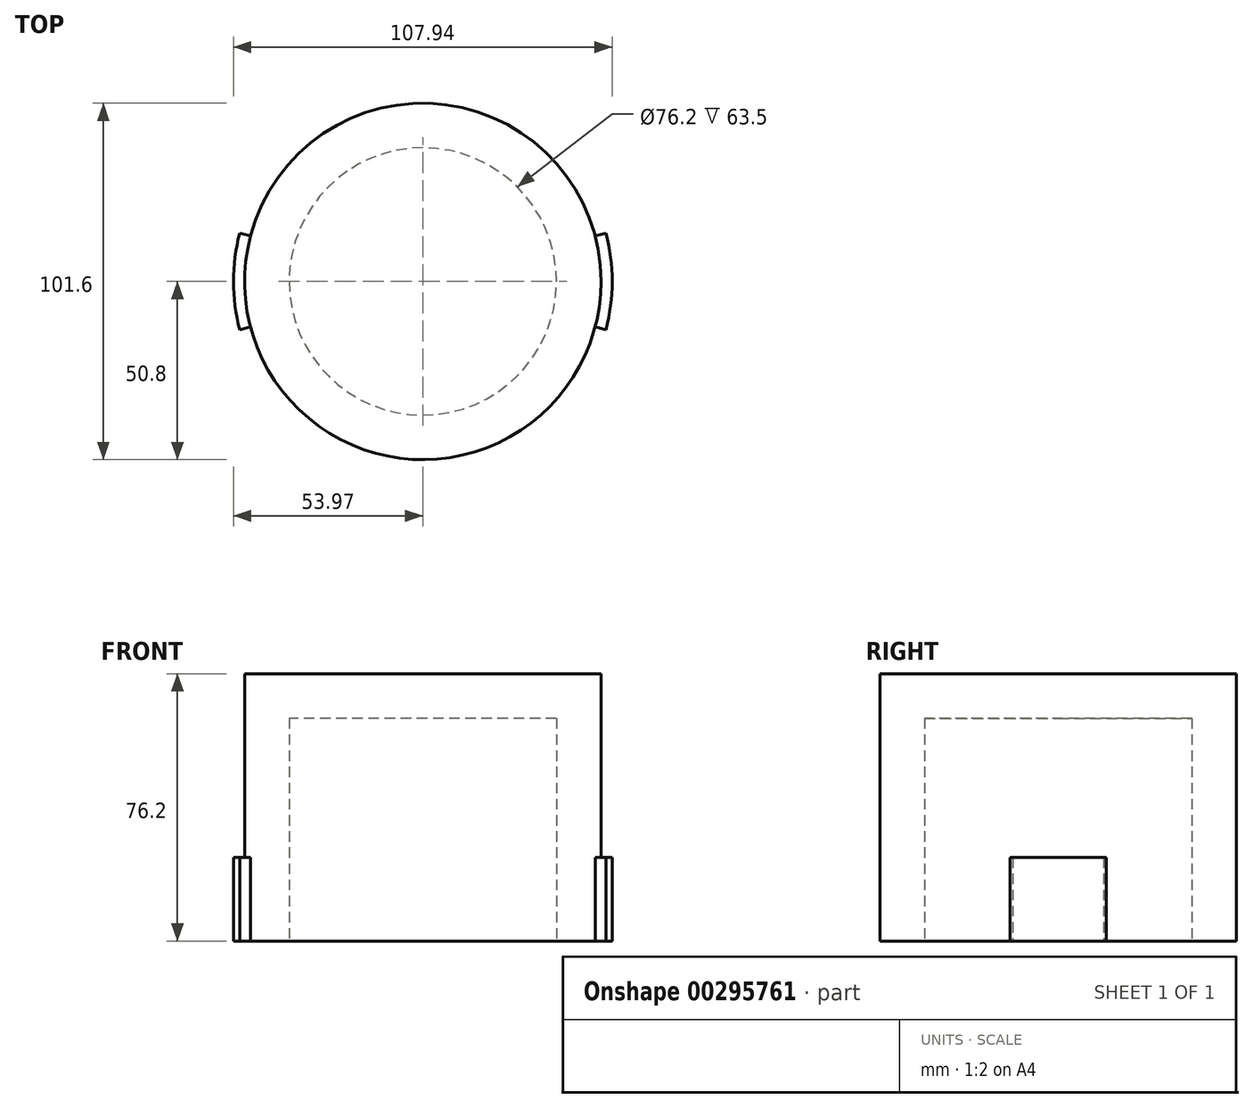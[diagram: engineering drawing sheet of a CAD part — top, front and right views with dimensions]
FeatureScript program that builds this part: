
annotation { "Feature Type Name" : "Feature", "Feature Type Description" : "" }
export const myFeature = defineFeature(function(context is Context, id is Id, definition is map)
    precondition{}
    {
        {
            var Q0;
            Q0=qCreatedBy(makeId("Top.planeOp"),FACE);
            var sketch = newSketch(context, id + "F0", { "sketchPlane" : qUnion([Q0])});
            skCircle(sketch, "E0", {"center": v(0, 0) * mm, "radius": 38.1 * mm});
            skCircle(sketch, "E1", {"center": v(0, 0) * mm, "radius": 50.8 * mm});
            skArc(sketch, "E2", {"start": v(52.2, -13.74) * mm, "mid": v(53.98, 0) * mm, "end": v(52.2, 13.74) * mm});
            skLineSegment(sketch, "E3", {"start": v(-49.13, -12.93) * mm, "end": v(-52.2, -13.74) * mm});
            skLineSegment(sketch, "E4.MirrorCS", {"start": v(49.13, -12.93) * mm, "end": v(52.2, -13.74) * mm});
            skLineSegment(sketch, "E5.MirrorCS", {"start": v(49.13, 12.93) * mm, "end": v(52.2, 13.74) * mm});
            skLineSegment(sketch, "E6.trimOffspring", {"start": v(-49.13, 12.93) * mm, "end": v(-52.2, 13.74) * mm});
            skArc(sketch, "E7.trimOffspring", {"start": v(-52.2, 13.74) * mm, "mid": v(-53.98, 0) * mm, "end": v(-52.2, -13.74) * mm});
            skSolve(sketch);
        }
        {
            var Q0;
            Q0=makeQuery(id+"F0.imprint","IMPRINT",FACE,{"disambiguationData":[TD([[makeQuery(id+"F0.imprint","IMPRINT",EDGE,{"derivedFrom":sQuery(id+"F0.wireOp",EDGE,"E0")}),1.0]])]});
            var Q1;
            Q1=makeQuery(id+"F0.imprint","IMPRINT",FACE,{"disambiguationData":[TD([[makeQuery(id+"F0.imprint","IMPRINT",EDGE,{"derivedFrom":sQuery(id+"F0.wireOp",EDGE,"E0")}),-1.0]])]});
            extrude(context, id + "F1", {"entities" : qUnion([Q0, Q1]), "depth" : 76.2 * mm});
        }
        {
            var Q0;
            {var subQ0=sQuery(id+"F0.wireOp",EDGE,"E3");Q0=makeQuery(id+"F0.imprint","IMPRINT",FACE,{"disambiguationData":[TD([[makeQuery(id+"F0.imprint","IMPRINT",EDGE,{"derivedFrom":subQ0}),-1.0]])]});}
            var Q1;
            Q1=makeQuery(id+"F0.imprint","IMPRINT",FACE,{"disambiguationData":[TD([[makeQuery(id+"F0.imprint","IMPRINT",EDGE,{"derivedFrom":sQuery(id+"F0.wireOp",EDGE,"E2")}),1.0]])]});
            extrude(context, id + "F2", {"entities" : qUnion([Q0, Q1]), "operationType" : NewBodyOperationType.ADD, "depth" : 23.8 * mm});
        }
        {
            var Q0;
            Q0=makeQuery(id+"F0.imprint","IMPRINT",FACE,{"disambiguationData":[TD([[makeQuery(id+"F0.imprint","IMPRINT",EDGE,{"derivedFrom":sQuery(id+"F0.wireOp",EDGE,"E0")}),1.0]])]});
            extrude(context, id + "F3", {"entities" : qUnion([Q0]), "operationType" : NewBodyOperationType.REMOVE, "depth" : 63.5 * mm});
        }
    });
